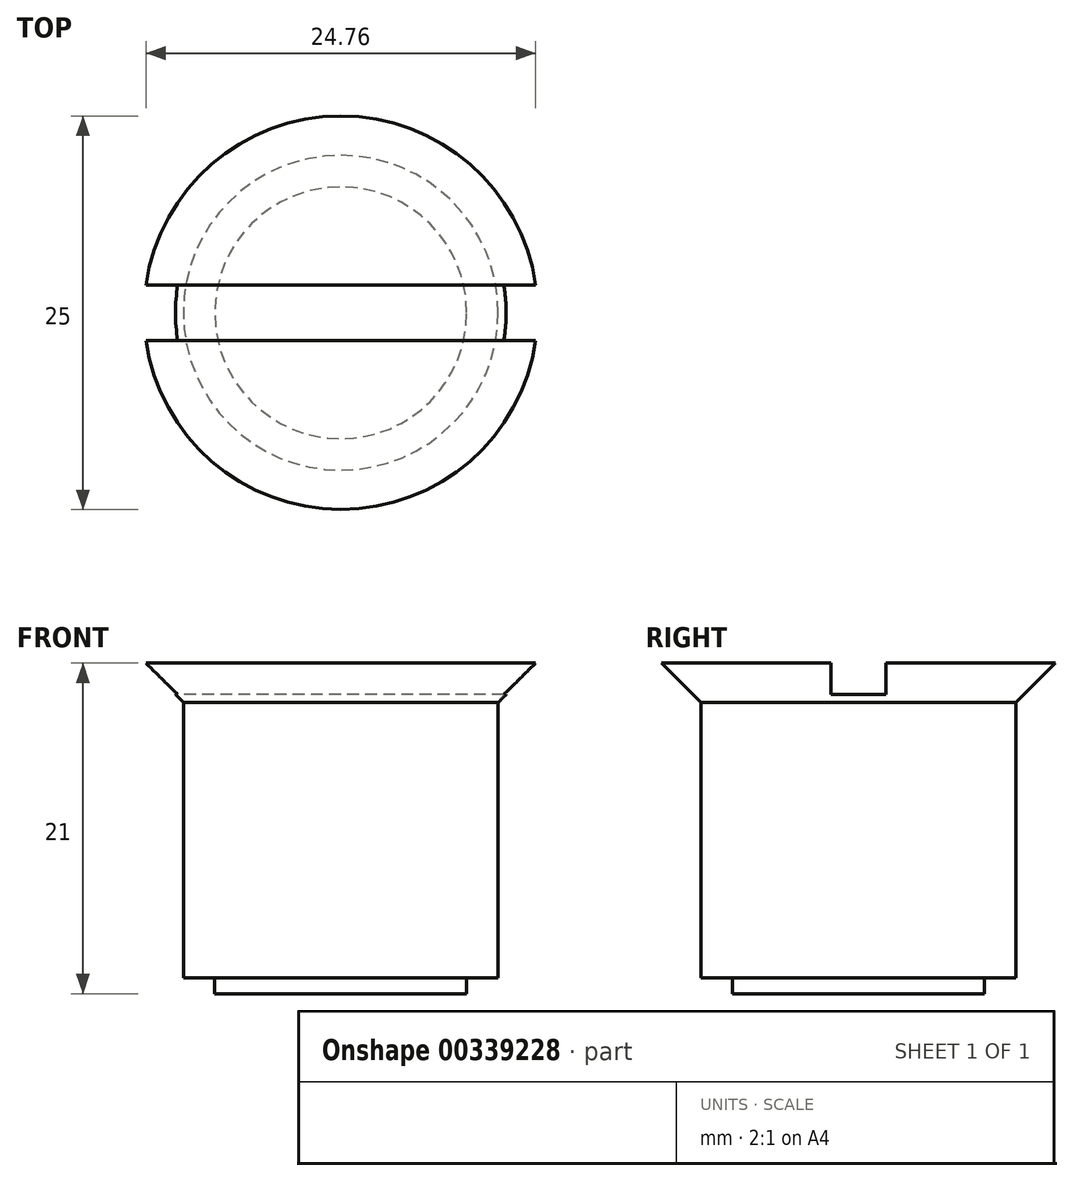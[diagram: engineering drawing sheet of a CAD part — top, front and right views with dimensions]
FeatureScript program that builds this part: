
annotation { "Feature Type Name" : "Feature", "Feature Type Description" : "" }
export const myFeature = defineFeature(function(context is Context, id is Id, definition is map)
    precondition{}
    {
        {
            var Q0;
            Q0=qCreatedBy(makeId("Front.planeOp"),FACE);
            var sketch = newSketch(context, id + "F0", { "sketchPlane" : qUnion([Q0])});
            skLineSegment(sketch, "E0", {"start": v(0, 0) * mm, "end": v(12.5, 0) * mm});
            skLineSegment(sketch, "E1", {"start": v(12.5, 0) * mm, "end": v(10, -2.5) * mm});
            skLineSegment(sketch, "E2", {"start": v(10, -2.5) * mm, "end": v(10, -20) * mm});
            skLineSegment(sketch, "E3", {"start": v(10, -20) * mm, "end": v(8, -20) * mm});
            skLineSegment(sketch, "E4", {"start": v(8, -20) * mm, "end": v(8, -21) * mm});
            skLineSegment(sketch, "E5", {"start": v(8, -21) * mm, "end": v(0, -21) * mm});
            skLineSegment(sketch, "E6", {"start": v(0, 0) * mm, "end": v(0, -21) * mm});
            skLineSegment(sketch, "E7", {"start": v(0, 0) * mm, "end": v(0, -25.3) * mm, "construction": true});
            skSolve(sketch);
        }
        {
            var Q0;
            Q0 = qSketchRegion(id + "F0", true);
            var Q1;
            Q1=sQuery(id+"F0.wireOp",EDGE,"E7");
            revolve(context, id + "F1", {"entities" : qUnion([Q0]), "axis" : qUnion([Q1]), "revolveType" : RevolveType.FULL});
        }
        {
            var Q0;
            Q0=makeQuery(id+"F1.opRevolve","SWEPT_FACE",FACE,{"disambiguationData":[OSD([sQuery(id+"F0.wireOp",EDGE,"E0")])]});
            var sketch = newSketch(context, id + "F2", { "sketchPlane" : qUnion([Q0])});
            skLineSegment(sketch, "E8.bottom", {"start": v(16.18, 1.75) * mm, "end": v(-13.82, 1.75) * mm});
            skLineSegment(sketch, "E8.top", {"start": v(16.18, -1.75) * mm, "end": v(-13.82, -1.75) * mm});
            skLineSegment(sketch, "E8.left", {"start": v(16.18, 1.75) * mm, "end": v(16.18, -1.75) * mm});
            skLineSegment(sketch, "E8.right", {"start": v(-13.82, 1.75) * mm, "end": v(-13.82, -1.75) * mm});
            skLineSegment(sketch, "E9", {"start": v(12.5, 0) * mm, "end": v(-12.5, 0) * mm, "construction": true});
            skSolve(sketch);
        }
        {
            var Q0;
            Q0 = qSketchRegion(id + "F2", true);
            extrude(context, id + "F3", {"entities" : qUnion([Q0]), "operationType" : NewBodyOperationType.REMOVE, "oppositeDirection" : true, "depth" : 2 * mm});
        }
    });
